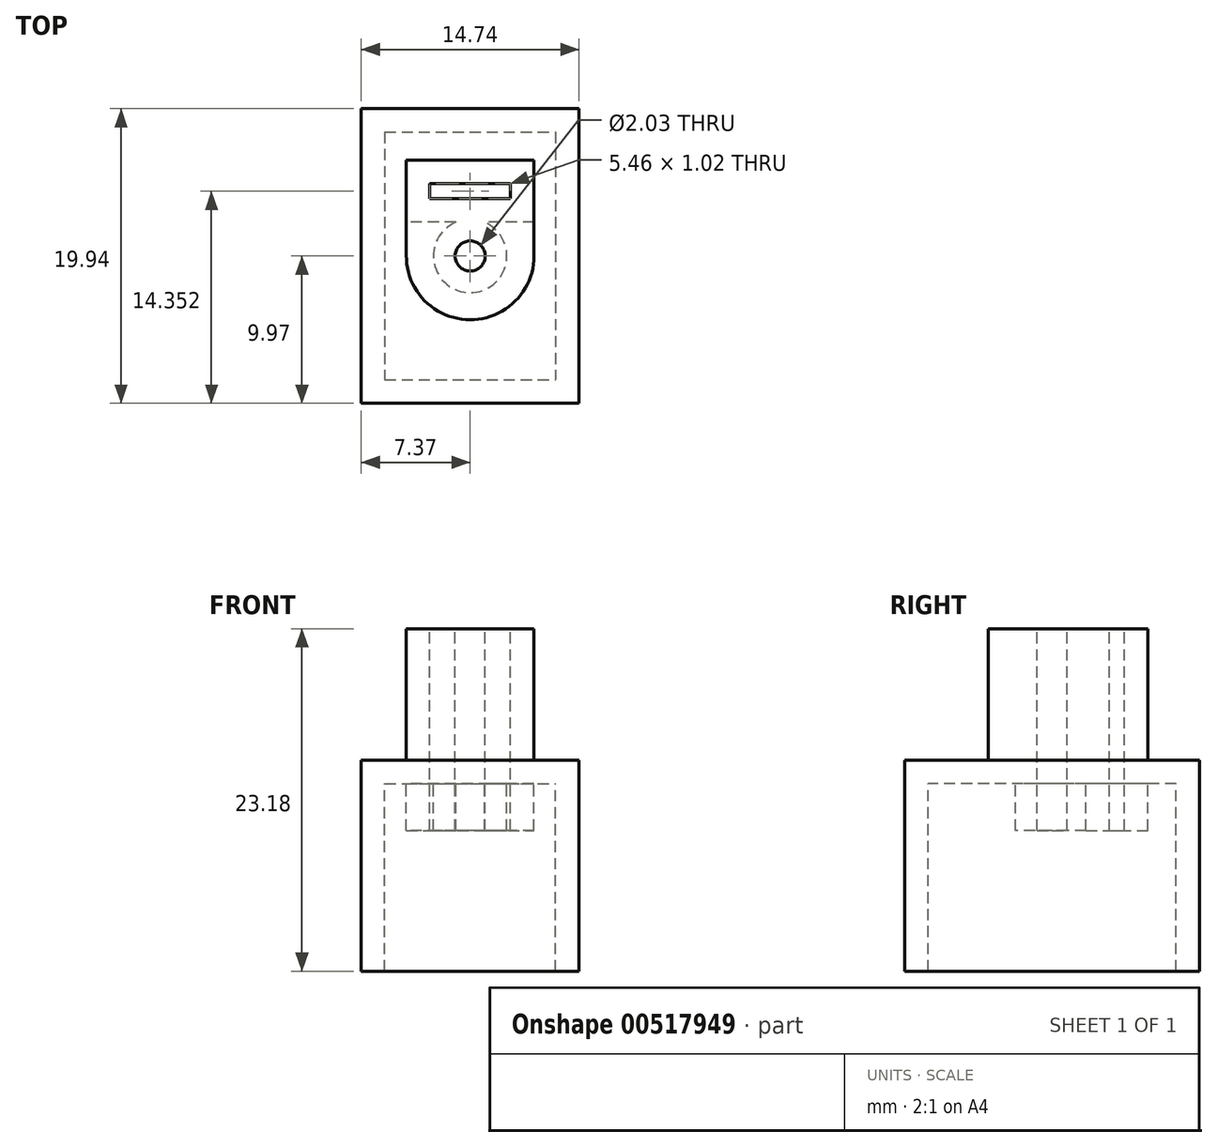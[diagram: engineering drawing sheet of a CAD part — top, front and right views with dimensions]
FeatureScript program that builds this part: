
annotation { "Feature Type Name" : "Feature", "Feature Type Description" : "" }
export const myFeature = defineFeature(function(context is Context, id is Id, definition is map)
    precondition{}
    {
        {
            var Q0;
            Q0=qCreatedBy(makeId("Top.planeOp"),FACE);
            var sketch = newSketch(context, id + "F0", { "sketchPlane" : qUnion([Q0])});
            skLineSegment(sketch, "E0", {"start": v(-4.32, 0) * mm, "end": v(-4.32, 6.48) * mm});
            skLineSegment(sketch, "E1", {"start": v(-4.32, 6.48) * mm, "end": v(4.32, 6.48) * mm});
            skLineSegment(sketch, "E2", {"start": v(4.32, 6.48) * mm, "end": v(4.32, 0) * mm});
            skArc(sketch, "E3", {"start": v(4.32, 0) * mm, "mid": v(-0.02, -4.32) * mm, "end": v(-4.32, 0.03) * mm});
            skLineSegment(sketch, "E4.0", {"start": v(2.73, 4.89) * mm, "end": v(2.73, 0) * mm});
            skLineSegment(sketch, "E4.1", {"start": v(-2.73, 4.89) * mm, "end": v(2.73, 4.89) * mm});
            skLineSegment(sketch, "E4.2", {"start": v(-2.73, 0) * mm, "end": v(-2.73, 4.89) * mm});
            skArc(sketch, "E5.0", {"start": v(2.73, 0) * mm, "mid": v(-0.01, -2.73) * mm, "end": v(-2.73, 0.02) * mm});
            skCircle(sketch, "E6", {"center": v(0, 0) * mm, "radius": 1.02 * mm});
            skLineSegment(sketch, "E7", {"start": v(2.73, 3.87) * mm, "end": v(-2.73, 3.87) * mm});
            skLineSegment(sketch, "E8.bottom", {"start": v(-7.37, 9.97) * mm, "end": v(7.37, 9.97) * mm});
            skLineSegment(sketch, "E8.top", {"start": v(-7.37, -9.97) * mm, "end": v(7.37, -9.97) * mm});
            skLineSegment(sketch, "E8.left", {"start": v(-7.37, 9.97) * mm, "end": v(-7.37, -9.97) * mm});
            skLineSegment(sketch, "E8.right", {"start": v(7.37, 9.97) * mm, "end": v(7.37, -9.97) * mm});
            skSolve(sketch);
        }
        {
            var Q0;
            {var subQ10=sQuery(id+"F0.wireOp",EDGE,"E0");Q0=makeQuery(id+"F0.imprint","IMPRINT",FACE,{"disambiguationData":[TD([[makeQuery(id+"F0.imprint","IMPRINT",EDGE,{"derivedFrom":subQ10}),-1.0]])]});}
            var Q1;
            Q1=makeQuery(id+"F0.imprint","IMPRINT",FACE,{"disambiguationData":[TD([[makeQuery(id+"F0.imprint","IMPRINT",EDGE,{"derivedFrom":sQuery(id+"F0.wireOp",EDGE,"E6")}),-1.0]])]});
            var Q2;
            {var subQ3=sQuery(id+"F0.wireOp",EDGE,"E0");Q2=makeQuery(id+"F0.imprint","IMPRINT",FACE,{"disambiguationData":[TD([[makeQuery(id+"F0.imprint","IMPRINT",EDGE,{"derivedFrom":subQ3}),1.0]])]});}
            extrude(context, id + "F1", {"entities" : qUnion([Q0, Q1, Q2]), "oppositeDirection" : true, "depth" : 1.59 * mm, "offsetDistance" : 25.4 * mm});
        }
        {
            var Q0;
            {var subQ10=sQuery(id+"F0.wireOp",EDGE,"E0");Q0=makeQuery(id+"F0.imprint","IMPRINT",FACE,{"disambiguationData":[TD([[makeQuery(id+"F0.imprint","IMPRINT",EDGE,{"derivedFrom":subQ10}),-1.0]])]});}
            extrude(context, id + "F2", {"entities" : qUnion([Q0]), "operationType" : NewBodyOperationType.ADD, "depth" : 8.9 * mm, "offsetDistance" : 25.4 * mm});
        }
        {
            var Q0;
            Q0=makeQuery(id+"F1.opExtrude","CAP_FACE",FACE,{"disambiguationData":[OSD([sQuery(id+"F0.wireOp",EDGE,"E4.0"),sQuery(id+"F0.wireOp",EDGE,"E4.1"),sQuery(id+"F0.wireOp",EDGE,"E4.2"),sQuery(id+"F0.wireOp",EDGE,"E6"),sQuery(id+"F0.wireOp",EDGE,"E7"),sQuery(id+"F0.wireOp",EDGE,"E8.bottom"),sQuery(id+"F0.wireOp",EDGE,"E8.top"),sQuery(id+"F0.wireOp",EDGE,"E8.left"),sQuery(id+"F0.wireOp",EDGE,"E8.right")])],"isStart":false});
            var sketch = newSketch(context, id + "F3", { "sketchPlane" : qUnion([Q0])});
            skLineSegment(sketch, "E9.0", {"start": v(-5.78, -8.38) * mm, "end": v(5.78, -8.38) * mm});
            skLineSegment(sketch, "E9.1", {"start": v(-5.78, -8.38) * mm, "end": v(-5.78, 8.38) * mm});
            skLineSegment(sketch, "E9.2", {"start": v(-5.78, 8.38) * mm, "end": v(5.78, 8.38) * mm});
            skLineSegment(sketch, "E9.3", {"start": v(5.78, -8.38) * mm, "end": v(5.78, 8.38) * mm});
            skCircle(sketch, "E10", {"center": v(0, 0) * mm, "radius": 2.48 * mm});
            skLineSegment(sketch, "E11.0", {"start": v(-4.32, -6.48) * mm, "end": v(4.32, -6.48) * mm});
            skLineSegment(sketch, "E11.1", {"start": v(-4.32, -2.29) * mm, "end": v(-4.32, -6.48) * mm});
            skLineSegment(sketch, "E11.2", {"start": v(4.32, -2.29) * mm, "end": v(-4.32, -2.29) * mm});
            skLineSegment(sketch, "E11.3", {"start": v(4.32, -6.48) * mm, "end": v(4.32, -2.29) * mm});
            skSolve(sketch);
        }
        {
            var Q0;
            Q0=makeQuery(id+"F3.imprint","IMPRINT",FACE,{"disambiguationData":[TD([[makeQuery(id+"F3.imprint","IMPRINT",EDGE,{"derivedFrom":sQuery(id+"F3.wireOp",EDGE,"E9.0")}),-1.0]])]});
            var Q1;
            Q1=makeQuery(id+"F3.imprint","IMPRINT",FACE,{"disambiguationData":[TD([[makeQuery(id+"F3.imprint","IMPRINT",EDGE,{"derivedFrom":sQuery(id+"F3.wireOp",EDGE,"E10")}),1.0]])]});
            var Q2;
            Q2=makeQuery(id+"F3.imprint","IMPRINT",FACE,{"disambiguationData":[TD([[makeQuery(id+"F3.imprint","IMPRINT",EDGE,{"derivedFrom":makeQuery(id+"F1.opExtrude","CAP_EDGE",EDGE,{"disambiguationData":[OSD([sQuery(id+"F0.wireOp",EDGE,"E6")])],"isStart":false})}),1.0]])]});
            var Q3;
            Q3=makeQuery(id+"F3.imprint","IMPRINT",FACE,{"disambiguationData":[TD([[makeQuery(id+"F3.imprint","IMPRINT",EDGE,{"derivedFrom":sQuery(id+"F3.wireOp",EDGE,"E11.0")}),1.0]])]});
            extrude(context, id + "F4", {"entities" : qUnion([Q0, Q1, Q2, Q3]), "operationType" : NewBodyOperationType.ADD, "depth" : 3.17 * mm, "offsetDistance" : 25.4 * mm});
        }
        {
            var Q0;
            Q0=makeQuery(id+"F4.opExtrude","CAP_FACE",FACE,{"disambiguationData":[OSD([sQuery(id+"F0.wireOp",EDGE,"E8.bottom"),sQuery(id+"F0.wireOp",EDGE,"E8.top"),sQuery(id+"F0.wireOp",EDGE,"E8.left"),sQuery(id+"F0.wireOp",EDGE,"E8.right"),sQuery(id+"F3.wireOp",EDGE,"E9.0"),sQuery(id+"F3.wireOp",EDGE,"E9.1"),sQuery(id+"F3.wireOp",EDGE,"E9.2"),sQuery(id+"F3.wireOp",EDGE,"E9.3")])],"isStart":false});
            extrude(context, id + "F5", {"entities" : qUnion([Q0]), "operationType" : NewBodyOperationType.ADD, "depth" : 9.52 * mm, "offsetDistance" : 25.4 * mm});
        }
    });
